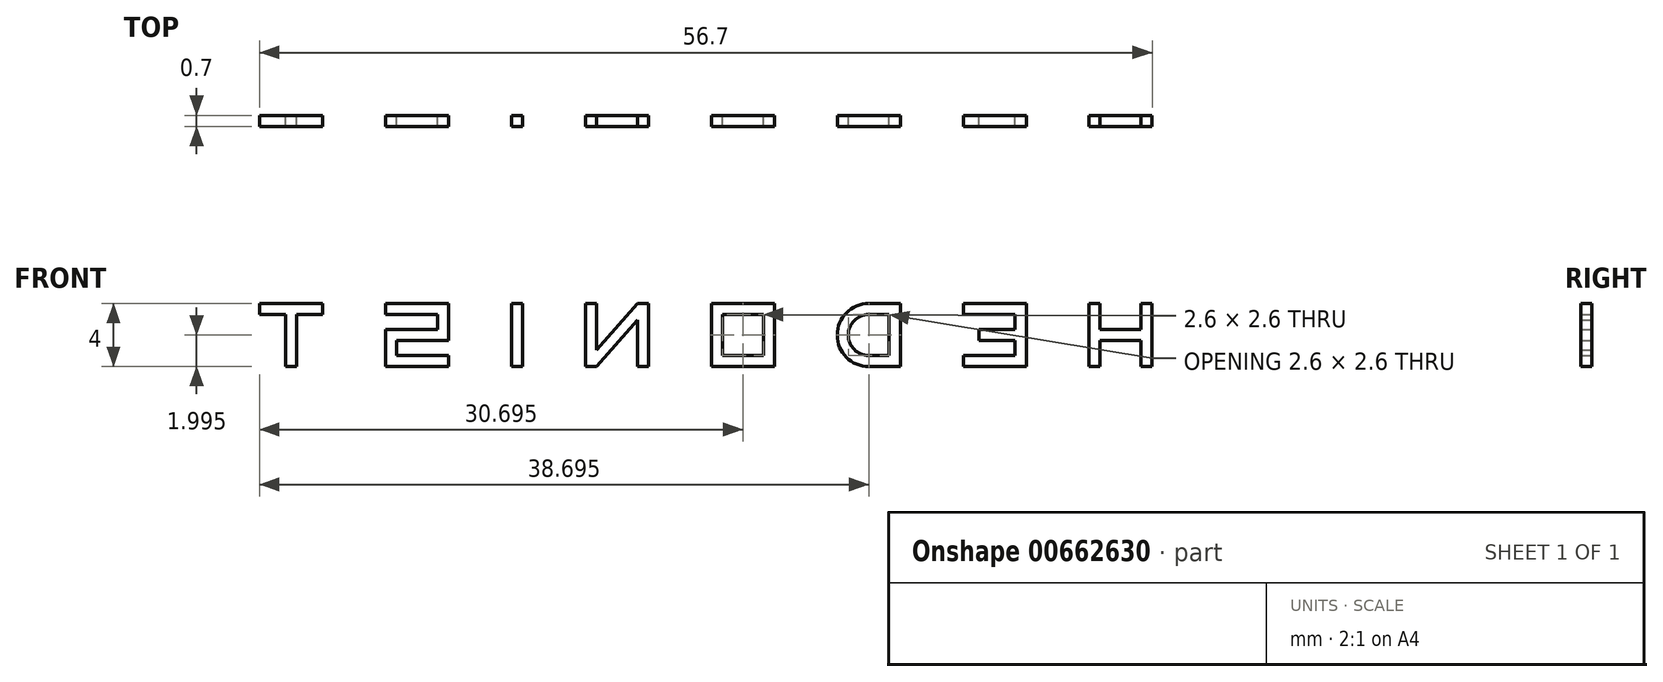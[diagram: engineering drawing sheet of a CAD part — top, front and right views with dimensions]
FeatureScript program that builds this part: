
annotation { "Feature Type Name" : "Feature", "Feature Type Description" : "" }
export const myFeature = defineFeature(function(context is Context, id is Id, definition is map)
    precondition{}
    {
        {
            var Q0;
            Q0=qCreatedBy(makeId("Front.planeOp"),FACE);
            var sketch = newSketch(context, id + "F0", { "sketchPlane" : qUnion([Q0])});
            skLineSegment(sketch, "E0.bottom", {"start": v(97.7, 129.52) * mm, "end": v(-112.3, 129.52) * mm, "construction": true});
            skLineSegment(sketch, "E0.top", {"start": v(97.7, -167.48) * mm, "end": v(-112.3, -167.48) * mm, "construction": true});
            skLineSegment(sketch, "E0.left", {"start": v(97.7, 129.52) * mm, "end": v(97.7, -167.48) * mm, "construction": true});
            skLineSegment(sketch, "E0.right", {"start": v(-112.3, 129.52) * mm, "end": v(-112.3, -167.48) * mm, "construction": true});
            skLineSegment(sketch, "E1.0", {"start": v(87.7, 129.52) * mm, "end": v(87.7, -167.48) * mm, "construction": true});
            skLineSegment(sketch, "E2.0", {"start": v(97.7, 119.52) * mm, "end": v(-112.3, 119.52) * mm, "construction": true});
            skLineSegment(sketch, "E3.0", {"start": v(-102.3, 129.52) * mm, "end": v(-102.3, -167.48) * mm, "construction": true});
            skLineSegment(sketch, "E4.0", {"start": v(97.7, -157.48) * mm, "end": v(-112.3, -157.48) * mm, "construction": true});
            skLineSegment(sketch, "E5.bottom", {"start": v(83.18, 113.17) * mm, "end": v(29.18, 113.17) * mm, "construction": true});
            skLineSegment(sketch, "E5.top", {"start": v(83.18, 109.17) * mm, "end": v(29.18, 109.17) * mm, "construction": true});
            skLineSegment(sketch, "E5.left", {"start": v(83.18, 113.17) * mm, "end": v(83.18, 109.17) * mm, "construction": true});
            skLineSegment(sketch, "E5.right", {"start": v(29.18, 113.17) * mm, "end": v(29.18, 109.17) * mm, "construction": true});
            skLineSegment(sketch, "E6", {"start": v(83.18, 113.17) * mm, "end": v(83.18, 109.17) * mm});
            skLineSegment(sketch, "E7", {"start": v(83.18, 109.17) * mm, "end": v(82.48, 109.17) * mm});
            skLineSegment(sketch, "E8", {"start": v(82.48, 109.17) * mm, "end": v(82.48, 110.82) * mm});
            skLineSegment(sketch, "E9", {"start": v(82.48, 110.82) * mm, "end": v(79.88, 110.82) * mm});
            skLineSegment(sketch, "E10", {"start": v(79.88, 110.82) * mm, "end": v(79.88, 109.17) * mm});
            skLineSegment(sketch, "E11", {"start": v(79.88, 109.17) * mm, "end": v(79.18, 109.17) * mm});
            skLineSegment(sketch, "E12", {"start": v(79.18, 109.17) * mm, "end": v(79.18, 113.17) * mm});
            skLineSegment(sketch, "E13", {"start": v(79.18, 113.17) * mm, "end": v(79.88, 113.17) * mm});
            skLineSegment(sketch, "E14", {"start": v(79.88, 113.17) * mm, "end": v(79.88, 111.52) * mm});
            skLineSegment(sketch, "E15", {"start": v(79.88, 111.52) * mm, "end": v(82.48, 111.52) * mm});
            skLineSegment(sketch, "E16", {"start": v(82.48, 111.52) * mm, "end": v(82.48, 113.17) * mm});
            skLineSegment(sketch, "E17", {"start": v(82.48, 113.17) * mm, "end": v(83.18, 113.17) * mm});
            skLineSegment(sketch, "E18", {"start": v(81.14, 111.17) * mm, "end": v(20.2, 111.17) * mm, "construction": true});
            skLineSegment(sketch, "E19.0", {"start": v(81.14, 110.82) * mm, "end": v(20.2, 110.82) * mm, "construction": true});
            skLineSegment(sketch, "E20.0", {"start": v(81.14, 111.52) * mm, "end": v(20.2, 111.52) * mm, "construction": true});
            skLineSegment(sketch, "E21", {"start": v(75.18, 113.17) * mm, "end": v(75.18, 109.17) * mm});
            skLineSegment(sketch, "E22", {"start": v(75.18, 109.17) * mm, "end": v(71.18, 109.17) * mm});
            skLineSegment(sketch, "E23", {"start": v(71.18, 109.17) * mm, "end": v(71.18, 109.87) * mm});
            skLineSegment(sketch, "E24", {"start": v(71.18, 109.87) * mm, "end": v(74.48, 109.87) * mm});
            skLineSegment(sketch, "E25", {"start": v(74.48, 109.87) * mm, "end": v(74.48, 110.82) * mm});
            skLineSegment(sketch, "E26", {"start": v(74.48, 110.82) * mm, "end": v(72.18, 110.82) * mm});
            skLineSegment(sketch, "E27", {"start": v(72.18, 110.82) * mm, "end": v(72.18, 111.52) * mm});
            skLineSegment(sketch, "E28", {"start": v(72.18, 111.52) * mm, "end": v(74.48, 111.52) * mm});
            skLineSegment(sketch, "E29", {"start": v(74.48, 111.52) * mm, "end": v(74.48, 112.47) * mm});
            skLineSegment(sketch, "E30", {"start": v(74.48, 112.47) * mm, "end": v(71.18, 112.47) * mm});
            skLineSegment(sketch, "E31", {"start": v(71.18, 112.47) * mm, "end": v(71.18, 113.17) * mm});
            skLineSegment(sketch, "E32", {"start": v(71.18, 113.17) * mm, "end": v(75.18, 113.17) * mm});
            skLineSegment(sketch, "E33", {"start": v(67.18, 113.17) * mm, "end": v(67.18, 109.17) * mm});
            skLineSegment(sketch, "E34", {"start": v(67.18, 109.17) * mm, "end": v(65.18, 109.17) * mm});
            skLineSegment(sketch, "E35", {"start": v(67.18, 113.17) * mm, "end": v(65.18, 113.17) * mm});
            skLineSegment(sketch, "E36", {"start": v(65.18, 113.17) * mm, "end": v(67.18, 113.17) * mm});
            skArc(sketch, "E37", {"start": v(65.18, 113.17) * mm, "mid": v(63.18, 111.17) * mm, "end": v(65.18, 109.17) * mm});
            skLineSegment(sketch, "E38.0", {"start": v(66.48, 112.47) * mm, "end": v(66.48, 109.87) * mm});
            skLineSegment(sketch, "E39.0", {"start": v(65.18, 112.47) * mm, "end": v(66.48, 112.47) * mm});
            skLineSegment(sketch, "E40.0", {"start": v(66.48, 109.87) * mm, "end": v(65.18, 109.87) * mm});
            skArc(sketch, "E41", {"start": v(65.18, 112.47) * mm, "mid": v(63.88, 111.17) * mm, "end": v(65.18, 109.87) * mm});
            skLineSegment(sketch, "E42.bottom", {"start": v(59.18, 113.17) * mm, "end": v(55.18, 113.17) * mm});
            skLineSegment(sketch, "E42.top", {"start": v(59.18, 109.17) * mm, "end": v(55.18, 109.17) * mm});
            skLineSegment(sketch, "E42.left", {"start": v(59.18, 113.17) * mm, "end": v(59.18, 109.17) * mm});
            skLineSegment(sketch, "E42.right", {"start": v(55.18, 113.17) * mm, "end": v(55.18, 109.17) * mm});
            skLineSegment(sketch, "E43.bottom", {"start": v(58.48, 112.47) * mm, "end": v(55.88, 112.47) * mm});
            skLineSegment(sketch, "E43.top", {"start": v(58.48, 109.87) * mm, "end": v(55.88, 109.87) * mm});
            skLineSegment(sketch, "E43.left", {"start": v(58.48, 112.47) * mm, "end": v(58.48, 109.87) * mm});
            skLineSegment(sketch, "E43.right", {"start": v(55.88, 112.47) * mm, "end": v(55.88, 109.87) * mm});
            skLineSegment(sketch, "E44", {"start": v(51.18, 113.17) * mm, "end": v(51.18, 109.17) * mm});
            skLineSegment(sketch, "E45", {"start": v(51.18, 109.17) * mm, "end": v(50.48, 109.17) * mm});
            skLineSegment(sketch, "E46", {"start": v(50.48, 109.17) * mm, "end": v(50.48, 112.1) * mm});
            skLineSegment(sketch, "E47", {"start": v(50.48, 112.1) * mm, "end": v(47.88, 109.17) * mm});
            skLineSegment(sketch, "E48", {"start": v(47.88, 109.17) * mm, "end": v(47.18, 109.17) * mm});
            skLineSegment(sketch, "E49", {"start": v(47.18, 109.17) * mm, "end": v(47.18, 113.17) * mm});
            skLineSegment(sketch, "E50", {"start": v(47.18, 113.17) * mm, "end": v(47.88, 113.17) * mm});
            skLineSegment(sketch, "E51", {"start": v(47.88, 113.17) * mm, "end": v(47.88, 110.22) * mm});
            skLineSegment(sketch, "E52", {"start": v(47.88, 110.22) * mm, "end": v(50.48, 113.17) * mm});
            skLineSegment(sketch, "E53", {"start": v(50.48, 113.17) * mm, "end": v(51.18, 113.17) * mm});
            skLineSegment(sketch, "E54.bottom", {"start": v(43.18, 113.17) * mm, "end": v(42.48, 113.17) * mm});
            skLineSegment(sketch, "E54.top", {"start": v(43.18, 109.17) * mm, "end": v(42.48, 109.17) * mm});
            skLineSegment(sketch, "E54.left", {"start": v(43.18, 113.17) * mm, "end": v(43.18, 109.17) * mm});
            skLineSegment(sketch, "E54.right", {"start": v(42.48, 113.17) * mm, "end": v(42.48, 109.17) * mm});
            skLineSegment(sketch, "E55", {"start": v(34.48, 113.17) * mm, "end": v(38.48, 113.17) * mm});
            skLineSegment(sketch, "E56", {"start": v(38.48, 113.17) * mm, "end": v(38.48, 110.82) * mm});
            skLineSegment(sketch, "E57", {"start": v(38.48, 110.82) * mm, "end": v(35.18, 110.82) * mm});
            skLineSegment(sketch, "E58", {"start": v(35.18, 110.82) * mm, "end": v(35.18, 109.87) * mm});
            skLineSegment(sketch, "E59", {"start": v(35.18, 109.87) * mm, "end": v(38.48, 109.87) * mm});
            skLineSegment(sketch, "E60", {"start": v(38.48, 109.87) * mm, "end": v(38.48, 109.17) * mm});
            skLineSegment(sketch, "E61", {"start": v(38.48, 109.17) * mm, "end": v(34.48, 109.17) * mm});
            skLineSegment(sketch, "E62", {"start": v(34.48, 109.17) * mm, "end": v(34.48, 111.52) * mm});
            skLineSegment(sketch, "E63", {"start": v(34.48, 111.52) * mm, "end": v(37.78, 111.52) * mm});
            skLineSegment(sketch, "E64", {"start": v(37.78, 111.52) * mm, "end": v(37.78, 112.47) * mm});
            skLineSegment(sketch, "E65", {"start": v(37.78, 112.47) * mm, "end": v(34.48, 112.47) * mm});
            skLineSegment(sketch, "E66", {"start": v(34.48, 112.47) * mm, "end": v(34.48, 113.17) * mm});
            skLineSegment(sketch, "E67", {"start": v(30.48, 113.17) * mm, "end": v(30.48, 112.47) * mm});
            skLineSegment(sketch, "E68", {"start": v(30.48, 112.47) * mm, "end": v(28.83, 112.47) * mm});
            skLineSegment(sketch, "E69", {"start": v(28.83, 112.47) * mm, "end": v(28.83, 109.17) * mm});
            skLineSegment(sketch, "E70", {"start": v(28.83, 109.17) * mm, "end": v(28.13, 109.17) * mm});
            skLineSegment(sketch, "E71", {"start": v(28.13, 109.17) * mm, "end": v(28.13, 112.47) * mm});
            skLineSegment(sketch, "E72", {"start": v(28.13, 112.47) * mm, "end": v(26.48, 112.47) * mm});
            skLineSegment(sketch, "E73", {"start": v(26.48, 112.47) * mm, "end": v(26.48, 113.17) * mm});
            skLineSegment(sketch, "E74", {"start": v(26.48, 113.17) * mm, "end": v(30.48, 113.17) * mm});
            skSolve(sketch);
        }
        {
            var Q0;
            Q0=makeQuery(id+"F0.imprint","IMPRINT",FACE,{"disambiguationData":[TD([[makeQuery(id+"F0.imprint","IMPRINT",EDGE,{"derivedFrom":sQuery(id+"F0.wireOp",EDGE,"E6")}),-1.0]])]});
            var Q1;
            Q1=makeQuery(id+"F0.imprint","IMPRINT",FACE,{"disambiguationData":[TD([[makeQuery(id+"F0.imprint","IMPRINT",EDGE,{"derivedFrom":sQuery(id+"F0.wireOp",EDGE,"E21")}),-1.0]])]});
            var Q2;
            Q2=makeQuery(id+"F0.imprint","IMPRINT",FACE,{"disambiguationData":[TD([[makeQuery(id+"F0.imprint","IMPRINT",EDGE,{"derivedFrom":sQuery(id+"F0.wireOp",EDGE,"E33")}),-1.0]])]});
            var Q3;
            Q3=makeQuery(id+"F0.imprint","IMPRINT",FACE,{"disambiguationData":[TD([[makeQuery(id+"F0.imprint","IMPRINT",EDGE,{"derivedFrom":sQuery(id+"F0.wireOp",EDGE,"E42.bottom")}),1.0]])]});
            var Q4;
            Q4=makeQuery(id+"F0.imprint","IMPRINT",FACE,{"disambiguationData":[TD([[makeQuery(id+"F0.imprint","IMPRINT",EDGE,{"derivedFrom":sQuery(id+"F0.wireOp",EDGE,"E44")}),-1.0]])]});
            var Q5;
            Q5=makeQuery(id+"F0.imprint","IMPRINT",FACE,{"disambiguationData":[TD([[makeQuery(id+"F0.imprint","IMPRINT",EDGE,{"derivedFrom":sQuery(id+"F0.wireOp",EDGE,"E54.bottom")}),1.0]])]});
            var Q6;
            Q6=makeQuery(id+"F0.imprint","IMPRINT",FACE,{"disambiguationData":[TD([[makeQuery(id+"F0.imprint","IMPRINT",EDGE,{"derivedFrom":sQuery(id+"F0.wireOp",EDGE,"E55")}),-1.0]])]});
            var Q7;
            Q7=makeQuery(id+"F0.imprint","IMPRINT",FACE,{"disambiguationData":[TD([[makeQuery(id+"F0.imprint","IMPRINT",EDGE,{"derivedFrom":sQuery(id+"F0.wireOp",EDGE,"E67")}),-1.0]])]});
            extrude(context, id + "F1", {"entities" : qUnion([Q0, Q1, Q2, Q3, Q4, Q5, Q6, Q7]), "depth" : .7 * mm, "offsetDistance" : 25 * mm});
        }
    });
